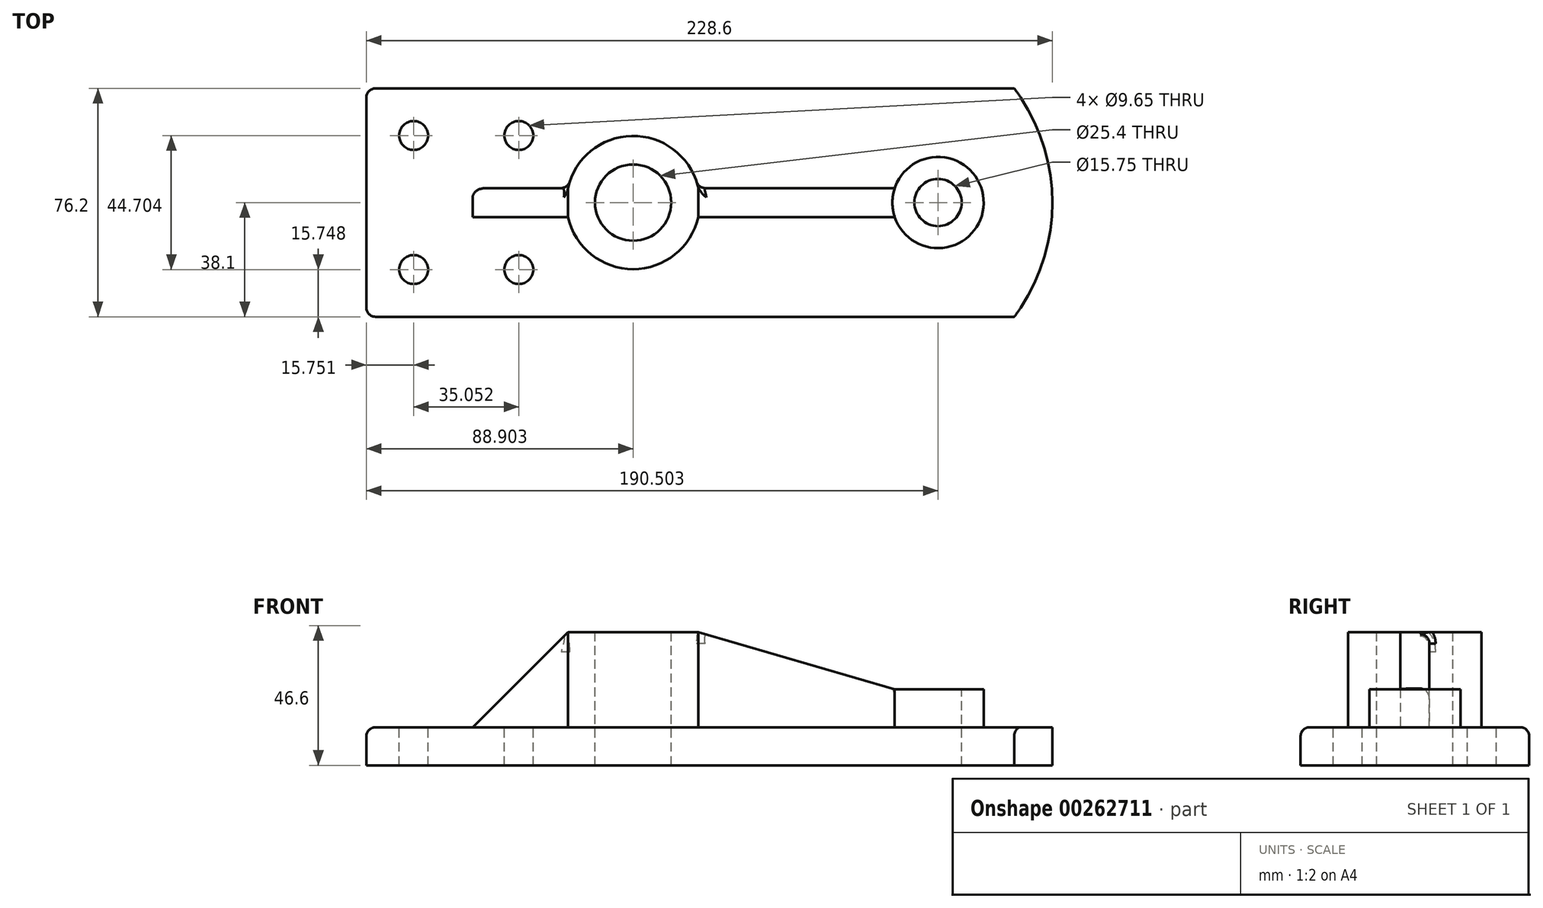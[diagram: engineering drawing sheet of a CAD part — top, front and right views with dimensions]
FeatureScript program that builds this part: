
annotation { "Feature Type Name" : "Feature", "Feature Type Description" : "" }
export const myFeature = defineFeature(function(context is Context, id is Id, definition is map)
    precondition{}
    {
        {
            var Q0;
            Q0=qCreatedBy(makeId("Top.planeOp"),FACE);
            var sketch = newSketch(context, id + "F0", { "sketchPlane" : qUnion([Q0])});
            skLineSegment(sketch, "E0", {"start": v(-126.57, 38.1) * mm, "end": v(-126.57, -38.1) * mm});
            skLineSegment(sketch, "E1", {"start": v(-126.57, -38.1) * mm, "end": v(89.33, -38.1) * mm});
            skLineSegment(sketch, "E2", {"start": v(-126.57, 38.1) * mm, "end": v(89.33, 38.1) * mm});
            skArc(sketch, "E3", {"start": v(89.33, -38.1) * mm, "mid": v(102.03, 0) * mm, "end": v(89.33, 38.1) * mm});
            skCircle(sketch, "E4", {"center": v(63.93, 0) * mm, "radius": 7.87 * mm});
            skCircle(sketch, "E5", {"center": v(63.93, 0) * mm, "radius": 15.21 * mm});
            skCircle(sketch, "E6", {"center": v(-37.67, 0) * mm, "radius": 12.7 * mm});
            skCircle(sketch, "E7", {"center": v(-37.67, 0) * mm, "radius": 22.23 * mm});
            skCircle(sketch, "E8", {"center": v(-110.82, 22.35) * mm, "radius": 4.83 * mm});
            skCircle(sketch, "E9", {"center": v(-75.77, 22.35) * mm, "radius": 4.83 * mm});
            skCircle(sketch, "E10", {"center": v(-110.82, -22.35) * mm, "radius": 4.83 * mm});
            skCircle(sketch, "E11", {"center": v(-75.77, -22.35) * mm, "radius": 4.83 * mm});
            skLineSegment(sketch, "E12", {"start": v(-15.97, 4.83) * mm, "end": v(49.5, 4.83) * mm});
            skLineSegment(sketch, "E13", {"start": v(-15.97, -4.83) * mm, "end": v(49.5, -4.83) * mm});
            skLineSegment(sketch, "E14", {"start": v(-59.36, 4.83) * mm, "end": v(-100.9, 4.83) * mm});
            skLineSegment(sketch, "E15", {"start": v(-100.9, 4.83) * mm, "end": v(-100.9, -4.83) * mm});
            skLineSegment(sketch, "E16", {"start": v(-100.9, -4.83) * mm, "end": v(-59.36, -4.83) * mm});
            skSolve(sketch);
        }
        {
            var Q0;
            Q0=makeQuery(id+"F0.imprint","IMPRINT",FACE,{"disambiguationData":[TD([[makeQuery(id+"F0.imprint","IMPRINT",EDGE,{"derivedFrom":sQuery(id+"F0.wireOp",EDGE,"E0")}),1.0]])]});
            var Q1;
            Q1=makeQuery(id+"F0.imprint","IMPRINT",FACE,{"disambiguationData":[TD([[makeQuery(id+"F0.imprint","IMPRINT",EDGE,{"derivedFrom":sQuery(id+"F0.wireOp",EDGE,"E6")}),-1.0]])]});
            var Q2;
            Q2=makeQuery(id+"F0.imprint","IMPRINT",FACE,{"disambiguationData":[TD([[makeQuery(id+"F0.imprint","IMPRINT",EDGE,{"derivedFrom":sQuery(id+"F0.wireOp",EDGE,"E4")}),-1.0]])]});
            var Q3;
            {var subQ0=sQuery(id+"F0.wireOp",EDGE,"E12");Q3=makeQuery(id+"F0.imprint","IMPRINT",FACE,{"disambiguationData":[TD([[makeQuery(id+"F0.imprint","IMPRINT",EDGE,{"derivedFrom":subQ0}),-1.0]])]});}
            var Q4;
            {var subQ0=sQuery(id+"F0.wireOp",EDGE,"E14");Q4=makeQuery(id+"F0.imprint","IMPRINT",FACE,{"disambiguationData":[TD([[makeQuery(id+"F0.imprint","IMPRINT",EDGE,{"derivedFrom":subQ0}),1.0]])]});}
            extrude(context, id + "F1", {"entities" : qUnion([Q0, Q1, Q2, Q3, Q4]), "oppositeDirection" : true, "depth" : 12.7 * mm});
        }
        {
            var Q0;
            Q0=makeQuery(id+"F0.imprint","IMPRINT",FACE,{"disambiguationData":[TD([[makeQuery(id+"F0.imprint","IMPRINT",EDGE,{"derivedFrom":sQuery(id+"F0.wireOp",EDGE,"E6")}),-1.0]])]});
            extrude(context, id + "F2", {"entities" : qUnion([Q0]), "operationType" : NewBodyOperationType.ADD, "depth" : 31.75 * mm});
        }
        {
            var Q0;
            Q0=makeQuery(id+"F0.imprint","IMPRINT",FACE,{"disambiguationData":[TD([[makeQuery(id+"F0.imprint","IMPRINT",EDGE,{"derivedFrom":sQuery(id+"F0.wireOp",EDGE,"E4")}),-1.0]])]});
            extrude(context, id + "F3", {"entities" : qUnion([Q0]), "operationType" : NewBodyOperationType.ADD, "depth" : 12.7 * mm});
        }
        {
            var Q0;
            {var subQ0=sQuery(id+"F0.wireOp",EDGE,"E12");Q0=makeQuery(id+"F0.imprint","IMPRINT",FACE,{"disambiguationData":[TD([[makeQuery(id+"F0.imprint","IMPRINT",EDGE,{"derivedFrom":subQ0}),-1.0]])]});}
            var Q1;
            {var subQ0=sQuery(id+"F0.wireOp",EDGE,"E14");Q1=makeQuery(id+"F0.imprint","IMPRINT",FACE,{"disambiguationData":[TD([[makeQuery(id+"F0.imprint","IMPRINT",EDGE,{"derivedFrom":subQ0}),1.0]])]});}
            var Q2;
            Q2 = qSketchRegion(id + "F5", true);
            extrude(context, id + "F4", {"entities" : qUnion([Q0, Q1, Q2]), "operationType" : NewBodyOperationType.ADD, "depth" : 31.75 * mm});
        }
        {
            var Q0;
            Q0=makeQuery(id+"F4.opExtrude","SWEPT_FACE",FACE,{"disambiguationData":[OSD([sQuery(id+"F0.wireOp",EDGE,"E16")])]});
            var sketch = newSketch(context, id + "F5", { "sketchPlane" : qUnion([Q0])});
            skLineSegment(sketch, "E17", {"start": v(-91.11, 0) * mm, "end": v(-59.36, 31.75) * mm});
            skSolve(sketch);
        }
        {
            var Q0;
            Q0=makeQuery(id+"F4.opExtrude","SWEPT_FACE",FACE,{"disambiguationData":[OSD([sQuery(id+"F0.wireOp",EDGE,"E13")])]});
            var sketch = newSketch(context, id + "F6", { "sketchPlane" : qUnion([Q0])});
            skLineSegment(sketch, "E18", {"start": v(-15.97, 31.75) * mm, "end": v(49.5, 12.7) * mm});
            skSolve(sketch);
        }
        {
            var Q0;
            Q0=makeQuery(id+"F5.imprint","IMPRINT",FACE,{"disambiguationData":[TD([[makeQuery(id+"F5.imprint","IMPRINT",EDGE,{"derivedFrom":sQuery(id+"F5.wireOp",EDGE,"CeQyvaNs-UcQL-aRFG-Wjeh-ebmeTFcGc0lL")}),-1.0]])]});
            var Q1;
            Q1=makeQuery(id+"F6.imprint","IMPRINT",FACE,{"disambiguationData":[TD([[makeQuery(id+"F6.imprint","IMPRINT",EDGE,{"derivedFrom":sQuery(id+"F6.wireOp",EDGE,"E18")}),1.0]])]});
            var Q2;
            {var subQ0=sQuery(id+"F5.wireOp",EDGE,"E17");Q2=makeQuery(id+"F5.imprint","IMPRINT",FACE,{"disambiguationData":[TD([[makeQuery(id+"F5.imprint","IMPRINT",EDGE,{"derivedFrom":subQ0}),1.0]])]});}
            extrude(context, id + "F7", {"entities" : qUnion([Q0, Q1, Q2]), "operationType" : NewBodyOperationType.REMOVE, "oppositeDirection" : true, "depth" : 25.4 * mm});
        }
        {
            var Q0;
            Q0=makeQuery(id+"F1.opExtrude","CAP_EDGE",EDGE,{"disambiguationData":[OSD([sQuery(id+"F0.wireOp",EDGE,"E1")])],"isStart":true});
            var Q1;
            Q1=makeQuery(id+"F1.opExtrude","SWEPT_EDGE",EDGE,{"disambiguationData":[OSD([sQuery(id+"F0.wireOp",EDGE,"E0"),sQuery(id+"F0.wireOp",EDGE,"E1")])]});
            var Q2;
            Q2=makeQuery(id+"F1.opExtrude","CAP_EDGE",EDGE,{"disambiguationData":[OSD([sQuery(id+"F0.wireOp",EDGE,"E0")])],"isStart":true});
            var Q3;
            Q3=makeQuery(id+"F1.opExtrude","CAP_EDGE",EDGE,{"disambiguationData":[OSD([sQuery(id+"F0.wireOp",EDGE,"E2")])],"isStart":true});
            var Q4;
            Q4=makeQuery(id+"F4.opExtrude","CAP_EDGE",EDGE,{"disambiguationData":[OSD([sQuery(id+"F0.wireOp",EDGE,"E13")])],"isStart":true});
            var Q5;
            {var subQ0=sQuery(id+"F0.wireOp",EDGE,"E7");Q5=makeQuery(id+"F4.boolean.opBoolean","SPLIT",EDGE,{"disambiguationData":[TD([makeQuery(id+"F4.opExtrude","SWEPT_FACE",FACE,{"disambiguationData":[OSD([sQuery(id+"F0.wireOp",EDGE,"E13")])]})])],"derivedFrom":makeQuery(id+"F2.opExtrude","CAP_EDGE",EDGE,{"disambiguationData":[OSD([subQ0])],"isStart":true})});}
            var Q6;
            Q6=makeQuery(id+"F4.opExtrude","CAP_EDGE",EDGE,{"disambiguationData":[OSD([sQuery(id+"F0.wireOp",EDGE,"E16")])],"isStart":true});
            var Q7;
            Q7=makeQuery(id+"F7.boolean.opBoolean","COPY",EDGE,{"derivedFrom":makeQuery(id+"F7.opExtrude","CAP_EDGE",EDGE,{"disambiguationData":[OSD([sQuery(id+"F5.wireOp",EDGE,"E17")])],"isStart":true})});
            var Q8;
            Q8=makeQuery(id+"F7.boolean.opBoolean","INTERSECT",EDGE,{"derivedFrom":[makeQuery(id+"F4.opExtrude","SWEPT_FACE",FACE,{"disambiguationData":[OSD([sQuery(id+"F0.wireOp",EDGE,"E14")])]}),makeQuery(id+"F7.opExtrude","SWEPT_FACE",FACE,{"disambiguationData":[OSD([sQuery(id+"F5.wireOp",EDGE,"E17")])]})]});
            var Q9;
            Q9=makeQuery(id+"F4.opExtrude","CAP_EDGE",EDGE,{"disambiguationData":[OSD([sQuery(id+"F0.wireOp",EDGE,"E14")])],"isStart":true});
            var Q10;
            Q10=makeQuery(id+"F4.opExtrude","CAP_EDGE",EDGE,{"disambiguationData":[OSD([sQuery(id+"F0.wireOp",EDGE,"E12")])],"isStart":true});
            var Q11;
            {var subQ0=sQuery(id+"F0.wireOp",EDGE,"E7");Q11=makeQuery(id+"F4.boolean.opBoolean","SPLIT",EDGE,{"disambiguationData":[TD([makeQuery(id+"F4.opExtrude","SWEPT_FACE",FACE,{"disambiguationData":[OSD([sQuery(id+"F0.wireOp",EDGE,"E12")])]})])],"derivedFrom":makeQuery(id+"F2.opExtrude","CAP_EDGE",EDGE,{"disambiguationData":[OSD([subQ0])],"isStart":true})});}
            var Q12;
            Q12=makeQuery(id+"F3.opExtrude","CAP_EDGE",EDGE,{"disambiguationData":[OSD([sQuery(id+"F0.wireOp",EDGE,"E5")])],"isStart":true});
            var Q13;
            Q13=makeQuery(id+"F1.opExtrude","SWEPT_EDGE",EDGE,{"disambiguationData":[OSD([sQuery(id+"F0.wireOp",EDGE,"E0"),sQuery(id+"F0.wireOp",EDGE,"E2")])]});
            var Q14;
            Q14=makeQuery(id+"F7.boolean.opBoolean","COPY",EDGE,{"derivedFrom":makeQuery(id+"F7.opExtrude","CAP_EDGE",EDGE,{"disambiguationData":[OSD([sQuery(id+"F6.wireOp",EDGE,"E18")])],"isStart":true})});
            var Q15;
            Q15=makeQuery(id+"F7.boolean.opBoolean","INTERSECT",EDGE,{"derivedFrom":[makeQuery(id+"F4.opExtrude","SWEPT_FACE",FACE,{"disambiguationData":[OSD([sQuery(id+"F0.wireOp",EDGE,"E12")])]}),makeQuery(id+"F7.opExtrude","SWEPT_FACE",FACE,{"disambiguationData":[OSD([sQuery(id+"F6.wireOp",EDGE,"E18")])]})]});
            fillet(context, id + "F8", {"entities" : qUnion([Q0, Q1, Q2, Q3, Q4, Q5, Q6, Q7, Q8, Q9, Q10, Q11, Q12, Q13, Q14, Q15]), "radius" : 3.05 * mm, "tangentPropagation" : true, "allowEdgeOverflow" : false});
        }
        {
            var Q0;
            Q0=makeQuery(id+"F4.opExtrude","SWEPT_EDGE",EDGE,{"disambiguationData":[OSD([sQuery(id+"F0.wireOp",EDGE,"E7"),sQuery(id+"F0.wireOp",EDGE,"E16")])]});
            var Q1;
            Q1=makeQuery(id+"F4.opExtrude","SWEPT_EDGE",EDGE,{"disambiguationData":[OSD([sQuery(id+"F0.wireOp",EDGE,"E7"),sQuery(id+"F0.wireOp",EDGE,"E14")])]});
            var Q2;
            Q2=makeQuery(id+"F4.opExtrude","SWEPT_EDGE",EDGE,{"disambiguationData":[OSD([sQuery(id+"F0.wireOp",EDGE,"E7"),sQuery(id+"F0.wireOp",EDGE,"E12")])]});
            var Q3;
            Q3=makeQuery(id+"F4.opExtrude","SWEPT_EDGE",EDGE,{"disambiguationData":[OSD([sQuery(id+"F0.wireOp",EDGE,"E7"),sQuery(id+"F0.wireOp",EDGE,"E13")])]});
            fillet(context, id + "F9", {"entities" : qUnion([Q0, Q1, Q2, Q3]), "radius" : 3.05 * mm, "tangentPropagation" : true, "allowEdgeOverflow" : false});
        }
    });
